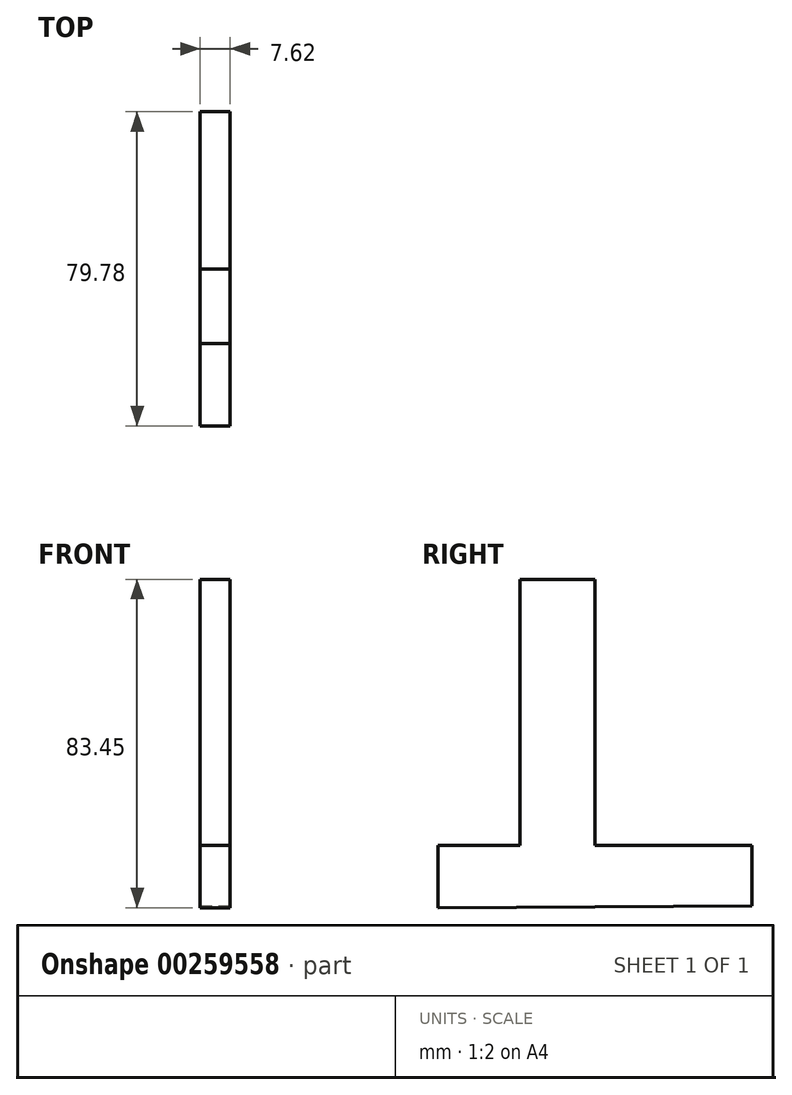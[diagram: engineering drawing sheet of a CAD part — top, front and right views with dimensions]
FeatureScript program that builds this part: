
annotation { "Feature Type Name" : "Feature", "Feature Type Description" : "" }
export const myFeature = defineFeature(function(context is Context, id is Id, definition is map)
    precondition{}
    {
        {
            var Q0;
            Q0=qCreatedBy(makeId("Right.planeOp"),FACE);
            var sketch = newSketch(context, id + "F1", { "sketchPlane" : qUnion([Q0])});
            skLineSegment(sketch, "E0", {"start": v(-30.8, -51.8) * mm, "end": v(-30.8, -51.8) * mm});
            skLineSegment(sketch, "E1", {"start": v(-30.8, -51.8) * mm, "end": v(48.98, -51.8) * mm});
            skLineSegment(sketch, "E2", {"start": v(48.98, -51.8) * mm, "end": v(-30.8, -51.8) * mm});
            skLineSegment(sketch, "E3", {"start": v(-30.8, -67.67) * mm, "end": v(-30.8, -67.67) * mm});
            skLineSegment(sketch, "E4", {"start": v(-30.8, -51.8) * mm, "end": v(-30.8, -67.67) * mm});
            skLineSegment(sketch, "E5", {"start": v(48.98, -51.8) * mm, "end": v(48.98, -67.15) * mm});
            skLineSegment(sketch, "E6", {"start": v(48.98, -67.15) * mm, "end": v(-30.8, -67.67) * mm});
            skLineSegment(sketch, "E7", {"start": v(-9.93, -51.8) * mm, "end": v(-9.93, 15.78) * mm});
            skLineSegment(sketch, "E8", {"start": v(9.09, -51.8) * mm, "end": v(9.09, 15.7) * mm});
            skLineSegment(sketch, "E9", {"start": v(9.09, 15.7) * mm, "end": v(-9.93, 15.78) * mm});
            skLineSegment(sketch, "E10", {"start": v(-9.93, 15.78) * mm, "end": v(23.92, 50.57) * mm});
            skLineSegment(sketch, "E11", {"start": v(-9.93, 15.78) * mm, "end": v(-40.51, -11.37) * mm});
            skLineSegment(sketch, "E12", {"start": v(-40.51, -11.37) * mm, "end": v(-50.6, 0) * mm});
            skSolve(sketch);
        }
        {
            var Q0;
            {var subQ0=sQuery(id+"F1.wireOp",EDGE,"E7");Q0=makeQuery(id+"F1.imprint","IMPRINT",FACE,{"disambiguationData":[TD([[makeQuery(id+"F1.imprint","IMPRINT",EDGE,{"derivedFrom":subQ0}),-1.0]])]});}
            var Q1;
            {var subQ0=sQuery(id+"F1.wireOp",EDGE,"E4");Q1=makeQuery(id+"F1.imprint","IMPRINT",FACE,{"disambiguationData":[TD([[makeQuery(id+"F1.imprint","IMPRINT",EDGE,{"derivedFrom":subQ0}),1.0]])]});}
            extrude(context, id + "F2", {"entities" : qUnion([Q0, Q1]), "oppositeDirection" : true, "depth" : 7.62 * mm});
        }
    });
